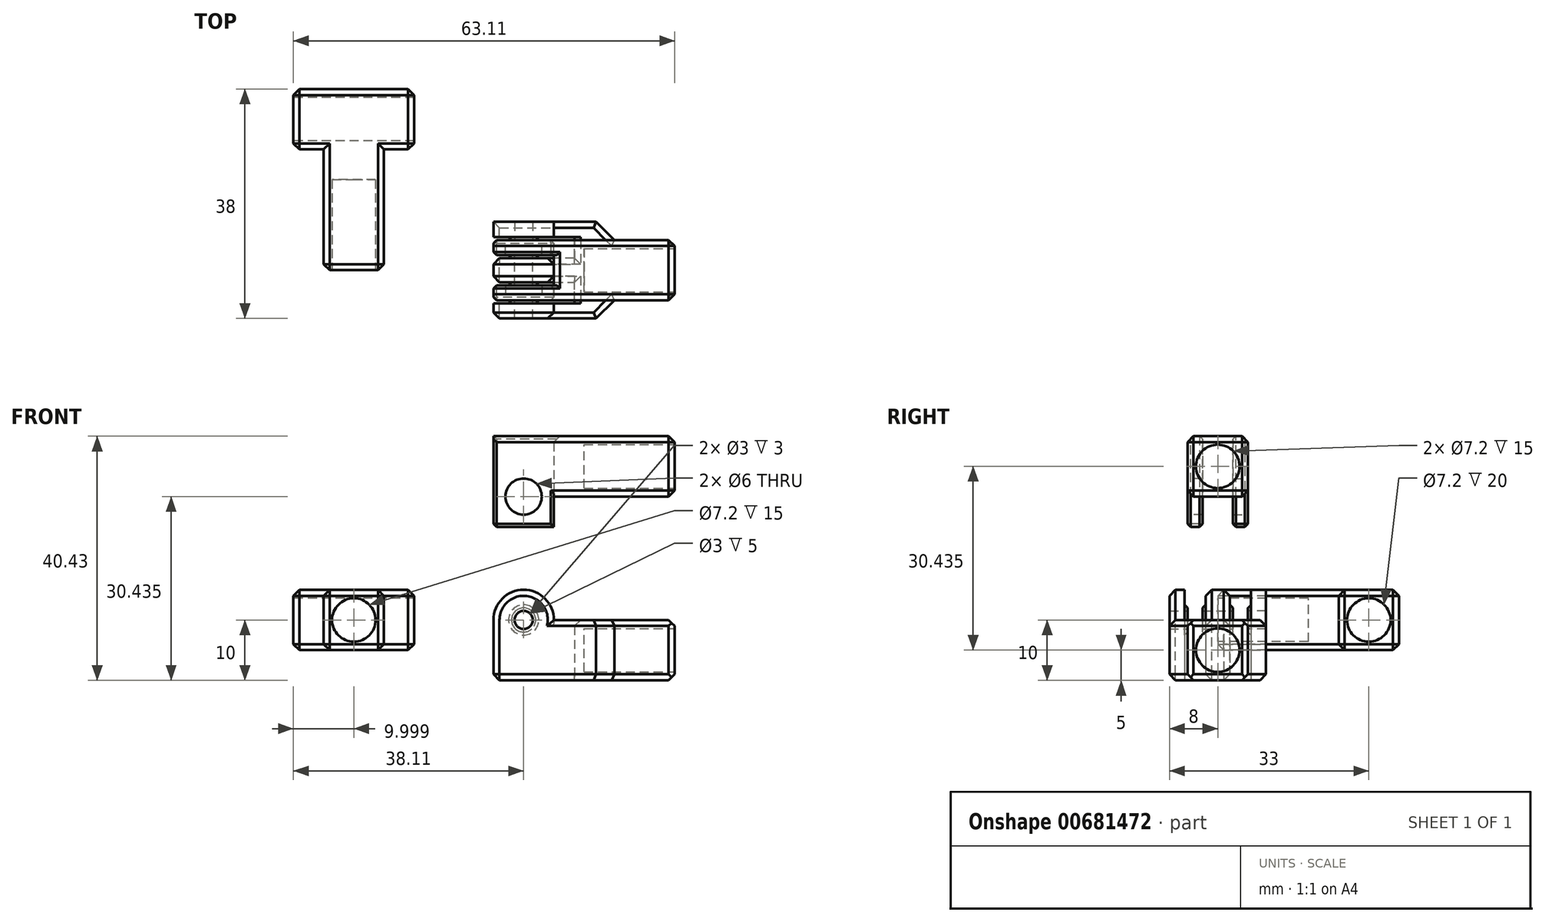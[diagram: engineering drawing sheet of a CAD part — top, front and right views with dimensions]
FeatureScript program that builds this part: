
annotation { "Feature Type Name" : "Feature", "Feature Type Description" : "" }
export const myFeature = defineFeature(function(context is Context, id is Id, definition is map)
    precondition{}
    {
        {
            var Q0;
            Q0=qCreatedBy(makeId("Front.planeOp"),FACE);
            var sketch = newSketch(context, id + "F0", { "sketchPlane" : qUnion([Q0])});
            skLineSegment(sketch, "E0.bottom", {"start": v(10, 5) * mm, "end": v(-10, 5) * mm});
            skLineSegment(sketch, "E0.top", {"start": v(10, -5) * mm, "end": v(-10, -5) * mm});
            skLineSegment(sketch, "E0.left", {"start": v(10, 5) * mm, "end": v(10, -5) * mm});
            skLineSegment(sketch, "E0.right", {"start": v(-10, 5) * mm, "end": v(-10, -5) * mm});
            skPoint(sketch, "E0.middle", {"position": v(0, 0) * mm});
            skSolve(sketch);
        }
        {
            var Q0;
            Q0 = qSketchRegion(id + "F0", true);
            extrude(context, id + "F1", {"entities" : qUnion([Q0]), "endBound" : BoundingType.SYMMETRIC, "depth" : 10 * mm, "offsetDistance" : 25 * mm});
        }
        {
            var Q0;
            Q0=qCreatedBy(makeId("Front.planeOp"),FACE);
            var sketch = newSketch(context, id + "F2", { "sketchPlane" : qUnion([Q0])});
            skLineSegment(sketch, "E1.bottom", {"start": v(-10, -5) * mm, "end": v(-20, -5) * mm});
            skLineSegment(sketch, "E1.top", {"start": v(-10, 10) * mm, "end": v(-20, 10) * mm});
            skLineSegment(sketch, "E1.left", {"start": v(-10, -5) * mm, "end": v(-10, 10) * mm});
            skLineSegment(sketch, "E1.right", {"start": v(-20, -5) * mm, "end": v(-20, 10) * mm});
            skPoint(sketch, "E2", {"position": v(-15, 5) * mm});
            skCircle(sketch, "E3", {"center": v(-15, 5) * mm, "radius": 1.5 * mm});
            skSolve(sketch);
        }
        {
            var Q0;
            Q0 = qSketchRegion(id + "F2", true);
            extrude(context, id + "F3", {"entities" : qUnion([Q0]), "operationType" : NewBodyOperationType.ADD, "endBound" : BoundingType.SYMMETRIC, "depth" : 4 * mm, "offsetDistance" : 25 * mm});
        }
        {
            var Q0;
            Q0=makeQuery(id+"F3.opExtrude","CAP_FACE",FACE,{"disambiguationData":[OSD([sQuery(id+"F2.wireOp",EDGE,"E1.bottom"),sQuery(id+"F2.wireOp",EDGE,"E1.top"),sQuery(id+"F2.wireOp",EDGE,"E1.left"),sQuery(id+"F2.wireOp",EDGE,"E1.right"),sQuery(id+"F2.wireOp",EDGE,"E3")])],"isStart":false});
            var sketch = newSketch(context, id + "F4", { "sketchPlane" : qUnion([Q0])});
            skCircle(sketch, "E4", {"center": v(-15, 5) * mm, "radius": 2.5 * mm});
            skCircle(sketch, "E5", {"center": v(-15, 5) * mm, "radius": 1.5 * mm});
            skSolve(sketch);
        }
        {
            var Q0;
            Q0 = qSketchRegion(id + "F4", true);
            extrude(context, id + "F5", {"entities" : qUnion([Q0]), "operationType" : NewBodyOperationType.ADD, "depth" : 0.5 * mm, "offsetDistance" : 25 * mm});
        }
        {
            var Q0;
            Q0=makeQuery(id+"F3.opExtrude","CAP_FACE",FACE,{"disambiguationData":[OSD([sQuery(id+"F2.wireOp",EDGE,"E1.bottom"),sQuery(id+"F2.wireOp",EDGE,"E1.top"),sQuery(id+"F2.wireOp",EDGE,"E1.left"),sQuery(id+"F2.wireOp",EDGE,"E1.right"),sQuery(id+"F2.wireOp",EDGE,"E3")])],"isStart":true});
            var sketch = newSketch(context, id + "F6", { "sketchPlane" : qUnion([Q0])});
            skCircle(sketch, "E6", {"center": v(15, 5) * mm, "radius": 2.5 * mm});
            skCircle(sketch, "E7", {"center": v(15, 5) * mm, "radius": 1.5 * mm});
            skSolve(sketch);
        }
        {
            var Q0;
            Q0 = qSketchRegion(id + "F6", true);
            extrude(context, id + "F7", {"entities" : qUnion([Q0]), "operationType" : NewBodyOperationType.ADD, "depth" : 0.5 * mm, "offsetDistance" : 25 * mm});
        }
        {
            var Q0;
            Q0=makeQuery(id+"F5.opExtrude","CAP_EDGE",EDGE,{"disambiguationData":[OSD([sQuery(id+"F4.wireOp",EDGE,"E4")])],"isStart":false});
            var Q1;
            Q1=makeQuery(id+"F7.opExtrude","CAP_EDGE",EDGE,{"disambiguationData":[OSD([sQuery(id+"F6.wireOp",EDGE,"E6")])],"isStart":false});
            chamfer(context, id + "F8", {"entities" : qUnion([Q0, Q1]), "width" : 0.5 * mm, "tangentPropagation" : true});
        }
        {
            var Q0;
            Q0=makeQuery(id+"F1.opExtrude","SWEPT_FACE",FACE,{"disambiguationData":[OSD([sQuery(id+"F0.wireOp",EDGE,"E0.left")])]});
            var sketch = newSketch(context, id + "F9", { "sketchPlane" : qUnion([Q0])});
            skCircle(sketch, "E8", {"center": v(0, 0) * mm, "radius": 3.6 * mm});
            skSolve(sketch);
        }
        {
            var Q0;
            Q0 = qSketchRegion(id + "F9", true);
            extrude(context, id + "F10", {"entities" : qUnion([Q0]), "operationType" : NewBodyOperationType.REMOVE, "oppositeDirection" : true, "depth" : 15 * mm, "offsetDistance" : 25 * mm});
        }
        {
            var Q0;
            Q0=makeQuery(id+"F1.opExtrude","CAP_EDGE",EDGE,{"disambiguationData":[OSD([sQuery(id+"F0.wireOp",EDGE,"E0.right")])],"isStart":false});
            var Q1;
            Q1=makeQuery(id+"F1.opExtrude","CAP_EDGE",EDGE,{"disambiguationData":[OSD([sQuery(id+"F0.wireOp",EDGE,"E0.right")])],"isStart":true});
            chamfer(context, id + "F11", {"entities" : qUnion([Q0, Q1]), "width" : 3 * mm, "tangentPropagation" : true});
        }
        {
            var Q0;
            Q0=makeQuery(id+"F3.opExtrude","CAP_EDGE",EDGE,{"disambiguationData":[OSD([sQuery(id+"F2.wireOp",EDGE,"E1.right")])],"isStart":false});
            var Q1;
            Q1=makeQuery(id+"F3.opExtrude","CAP_EDGE",EDGE,{"disambiguationData":[OSD([sQuery(id+"F2.wireOp",EDGE,"E1.right")])],"isStart":true});
            var Q2;
            Q2=makeQuery(id+"F1.opExtrude","CAP_EDGE",EDGE,{"disambiguationData":[OSD([sQuery(id+"F0.wireOp",EDGE,"E0.left")])],"isStart":true});
            var Q3;
            Q3=makeQuery(id+"F1.opExtrude","CAP_EDGE",EDGE,{"disambiguationData":[OSD([sQuery(id+"F0.wireOp",EDGE,"E0.left")])],"isStart":false});
            var Q4;
            Q4=makeQuery(id+"F1.opExtrude","SWEPT_EDGE",EDGE,{"disambiguationData":[OSD([sQuery(id+"F0.wireOp",EDGE,"E0.top"),sQuery(id+"F0.wireOp",EDGE,"E0.left")])]});
            var Q5;
            Q5=makeQuery(id+"F3.opExtrude","CAP_EDGE",EDGE,{"disambiguationData":[OSD([sQuery(id+"F2.wireOp",EDGE,"E1.bottom")])],"isStart":false});
            var Q6;
            Q6=makeQuery(id+"F3.opExtrude","CAP_EDGE",EDGE,{"disambiguationData":[OSD([sQuery(id+"F2.wireOp",EDGE,"E1.bottom")])],"isStart":true});
            var Q7;
            Q7=makeQuery(id+"F3.opExtrude","SWEPT_EDGE",EDGE,{"disambiguationData":[OSD([sQuery(id+"F2.wireOp",EDGE,"E1.bottom"),sQuery(id+"F2.wireOp",EDGE,"E1.right")])]});
            var Q8;
            Q8=makeQuery(id+"F1.opExtrude","SWEPT_EDGE",EDGE,{"disambiguationData":[OSD([sQuery(id+"F0.wireOp",EDGE,"E0.bottom"),sQuery(id+"F0.wireOp",EDGE,"E0.left")])]});
            chamfer(context, id + "F12", {"entities" : qUnion([Q0, Q1, Q2, Q3, Q4, Q5, Q6, Q7, Q8]), "width" : 1 * mm, "tangentPropagation" : true});
        }
        {
            var Q0;
            Q0=qCreatedBy(makeId("Front.planeOp"),FACE);
            var sketch = newSketch(context, id + "F13", { "sketchPlane" : qUnion([Q0])});
            skLineSegment(sketch, "E9.bottom", {"start": v(10, 25.43) * mm, "end": v(-10, 25.43) * mm});
            skLineSegment(sketch, "E9.top", {"start": v(10, 35.43) * mm, "end": v(-10, 35.43) * mm});
            skLineSegment(sketch, "E9.left", {"start": v(10, 25.43) * mm, "end": v(10, 35.43) * mm});
            skLineSegment(sketch, "E9.right", {"start": v(-10, 25.43) * mm, "end": v(-10, 35.43) * mm});
            skPoint(sketch, "E9.middle", {"position": v(0, 30.43) * mm});
            skSolve(sketch);
        }
        {
            var Q0;
            Q0 = qSketchRegion(id + "F13", true);
            extrude(context, id + "F14", {"entities" : qUnion([Q0]), "endBound" : BoundingType.SYMMETRIC, "depth" : 10 * mm, "offsetDistance" : 25 * mm});
        }
        {
            var Q0;
            Q0=makeQuery(id+"F14.opExtrude","CAP_FACE",FACE,{"disambiguationData":[OSD([sQuery(id+"F13.wireOp",EDGE,"E9.bottom"),sQuery(id+"F13.wireOp",EDGE,"E9.top"),sQuery(id+"F13.wireOp",EDGE,"E9.left"),sQuery(id+"F13.wireOp",EDGE,"E9.right")])],"isStart":true});
            var sketch = newSketch(context, id + "F15", { "sketchPlane" : qUnion([Q0])});
            skLineSegment(sketch, "E10.bottom", {"start": v(10, 35.43) * mm, "end": v(20, 35.43) * mm});
            skLineSegment(sketch, "E10.top", {"start": v(10, 20.43) * mm, "end": v(20, 20.43) * mm});
            skLineSegment(sketch, "E10.left", {"start": v(10, 35.43) * mm, "end": v(10, 20.43) * mm});
            skLineSegment(sketch, "E10.right", {"start": v(20, 35.43) * mm, "end": v(20, 20.43) * mm});
            skCircle(sketch, "E11", {"center": v(15, 25.43) * mm, "radius": 3 * mm});
            skSolve(sketch);
        }
        {
            var Q0;
            Q0 = qSketchRegion(id + "F15", true);
            extrude(context, id + "F16", {"entities" : qUnion([Q0]), "operationType" : NewBodyOperationType.ADD, "oppositeDirection" : true, "depth" : 2.5 * mm, "offsetDistance" : 25 * mm});
        }
        {
            var Q0;
            Q0=makeQuery(id+"F14.opExtrude","CAP_FACE",FACE,{"disambiguationData":[OSD([sQuery(id+"F13.wireOp",EDGE,"E9.bottom"),sQuery(id+"F13.wireOp",EDGE,"E9.top"),sQuery(id+"F13.wireOp",EDGE,"E9.left"),sQuery(id+"F13.wireOp",EDGE,"E9.right")])],"isStart":false});
            var sketch = newSketch(context, id + "F17", { "sketchPlane" : qUnion([Q0])});
            skLineSegment(sketch, "E12.bottom", {"start": v(-10, 35.43) * mm, "end": v(-20, 35.43) * mm});
            skLineSegment(sketch, "E12.top", {"start": v(-10, 20.43) * mm, "end": v(-20, 20.43) * mm});
            skLineSegment(sketch, "E12.left", {"start": v(-10, 35.43) * mm, "end": v(-10, 20.43) * mm});
            skLineSegment(sketch, "E12.right", {"start": v(-20, 35.43) * mm, "end": v(-20, 20.43) * mm});
            skCircle(sketch, "E13", {"center": v(-15, 25.43) * mm, "radius": 3 * mm});
            skSolve(sketch);
        }
        {
            var Q0;
            Q0 = qSketchRegion(id + "F17", true);
            extrude(context, id + "F18", {"entities" : qUnion([Q0]), "operationType" : NewBodyOperationType.ADD, "oppositeDirection" : true, "depth" : 2.5 * mm, "offsetDistance" : 25 * mm});
        }
        {
            var Q0;
            Q0=makeQuery(id+"F14.opExtrude","SWEPT_FACE",FACE,{"disambiguationData":[OSD([sQuery(id+"F13.wireOp",EDGE,"E9.left")])]});
            var sketch = newSketch(context, id + "F19", { "sketchPlane" : qUnion([Q0])});
            skCircle(sketch, "E14", {"center": v(0, 30.43) * mm, "radius": 3.6 * mm});
            skPoint(sketch, "E14.centerSnap0", {"position": v(-5, 30.43) * mm});
            skPoint(sketch, "E14.centerSnap1", {"position": v(0, 25.43) * mm});
            skSolve(sketch);
        }
        {
            var Q0;
            Q0 = qSketchRegion(id + "F19", true);
            extrude(context, id + "F20", {"entities" : qUnion([Q0]), "operationType" : NewBodyOperationType.REMOVE, "oppositeDirection" : true, "depth" : 15 * mm, "offsetDistance" : 25 * mm});
        }
        {
            var Q0;
            Q0=makeQuery(id+"F16.boolean.opBoolean","MERGE",EDGE,{"derivedFrom":[makeQuery(id+"F14.opExtrude","CAP_EDGE",EDGE,{"disambiguationData":[OSD([sQuery(id+"F13.wireOp",EDGE,"E9.top")])],"isStart":true}),makeQuery(id+"F16.opExtrude","CAP_EDGE",EDGE,{"disambiguationData":[OSD([sQuery(id+"F15.wireOp",EDGE,"E10.bottom")])],"isStart":true})]});
            var Q1;
            Q1=makeQuery(id+"F18.boolean.opBoolean","MERGE",EDGE,{"derivedFrom":[makeQuery(id+"F14.opExtrude","CAP_EDGE",EDGE,{"disambiguationData":[OSD([sQuery(id+"F13.wireOp",EDGE,"E9.top")])],"isStart":false}),makeQuery(id+"F18.opExtrude","CAP_EDGE",EDGE,{"disambiguationData":[OSD([sQuery(id+"F17.wireOp",EDGE,"E12.bottom")])],"isStart":true})]});
            var Q2;
            Q2=makeQuery(id+"F14.opExtrude","SWEPT_EDGE",EDGE,{"disambiguationData":[OSD([sQuery(id+"F13.wireOp",EDGE,"E9.top"),sQuery(id+"F13.wireOp",EDGE,"E9.left")])]});
            var Q3;
            Q3=makeQuery(id+"F14.opExtrude","SWEPT_EDGE",EDGE,{"disambiguationData":[OSD([sQuery(id+"F13.wireOp",EDGE,"E9.top"),sQuery(id+"F13.wireOp",EDGE,"E9.right")])]});
            var Q4;
            Q4=makeQuery(id+"F14.opExtrude","CAP_EDGE",EDGE,{"disambiguationData":[OSD([sQuery(id+"F13.wireOp",EDGE,"E9.bottom")])],"isStart":true});
            var Q5;
            Q5=makeQuery(id+"F14.opExtrude","CAP_EDGE",EDGE,{"disambiguationData":[OSD([sQuery(id+"F13.wireOp",EDGE,"E9.left")])],"isStart":true});
            var Q6;
            Q6=makeQuery(id+"F14.opExtrude","CAP_EDGE",EDGE,{"disambiguationData":[OSD([sQuery(id+"F13.wireOp",EDGE,"E9.bottom")])],"isStart":false});
            var Q7;
            Q7=makeQuery(id+"F14.opExtrude","CAP_EDGE",EDGE,{"disambiguationData":[OSD([sQuery(id+"F13.wireOp",EDGE,"E9.left")])],"isStart":false});
            var Q8;
            Q8=makeQuery(id+"F14.opExtrude","SWEPT_EDGE",EDGE,{"disambiguationData":[OSD([sQuery(id+"F13.wireOp",EDGE,"E9.bottom"),sQuery(id+"F13.wireOp",EDGE,"E9.left")])]});
            chamfer(context, id + "F21", {"entities" : qUnion([Q0, Q1, Q2, Q3, Q4, Q5, Q6, Q7, Q8]), "width" : 1 * mm, "tangentPropagation" : true});
        }
        {
            var Q0;
            Q0=makeQuery(id+"F18.opExtrude","CAP_EDGE",EDGE,{"disambiguationData":[OSD([sQuery(id+"F17.wireOp",EDGE,"E12.top")])],"isStart":true});
            var Q1;
            Q1=makeQuery(id+"F18.opExtrude","CAP_EDGE",EDGE,{"disambiguationData":[OSD([sQuery(id+"F17.wireOp",EDGE,"E12.top")])],"isStart":false});
            var Q2;
            Q2=makeQuery(id+"F18.opExtrude","CAP_EDGE",EDGE,{"disambiguationData":[OSD([sQuery(id+"F17.wireOp",EDGE,"E12.left")])],"isStart":true});
            var Q3;
            {var subQ0=sQuery(id+"F17.wireOp",EDGE,"E12.left");Q3=makeQuery(id+"F18.boolean.opBoolean","SPLIT",EDGE,{"disambiguationData":[topologyDisambiguationEdgeConnected([makeQuery(id+"F18.opExtrude","SWEPT_FACE",FACE,{"disambiguationData":[OSD([subQ0])]})])],"derivedFrom":makeQuery(id+"F18.opExtrude","CAP_EDGE",EDGE,{"disambiguationData":[OSD([subQ0])],"isStart":false})});}
            var Q4;
            Q4=makeQuery(id+"F18.opExtrude","CAP_EDGE",EDGE,{"disambiguationData":[OSD([sQuery(id+"F17.wireOp",EDGE,"E12.right")])],"isStart":true});
            var Q5;
            {var subQ0=sQuery(id+"F15.wireOp",EDGE,"E10.left");Q5=makeQuery(id+"F16.boolean.opBoolean","SPLIT",EDGE,{"disambiguationData":[topologyDisambiguationEdgeConnected([makeQuery(id+"F16.opExtrude","SWEPT_FACE",FACE,{"disambiguationData":[OSD([subQ0])]})])],"derivedFrom":makeQuery(id+"F16.opExtrude","CAP_EDGE",EDGE,{"disambiguationData":[OSD([subQ0])],"isStart":false})});}
            var Q6;
            Q6=makeQuery(id+"F16.opExtrude","CAP_EDGE",EDGE,{"disambiguationData":[OSD([sQuery(id+"F15.wireOp",EDGE,"E10.top")])],"isStart":false});
            var Q7;
            Q7=makeQuery(id+"F16.opExtrude","SWEPT_EDGE",EDGE,{"disambiguationData":[OSD([sQuery(id+"F15.wireOp",EDGE,"E10.top"),sQuery(id+"F15.wireOp",EDGE,"E10.left")])]});
            var Q8;
            Q8=makeQuery(id+"F16.opExtrude","CAP_EDGE",EDGE,{"disambiguationData":[OSD([sQuery(id+"F15.wireOp",EDGE,"E10.top")])],"isStart":true});
            var Q9;
            Q9=makeQuery(id+"F16.opExtrude","SWEPT_EDGE",EDGE,{"disambiguationData":[OSD([sQuery(id+"F15.wireOp",EDGE,"E10.top"),sQuery(id+"F15.wireOp",EDGE,"E10.right")])]});
            var Q10;
            Q10=makeQuery(id+"F18.opExtrude","SWEPT_EDGE",EDGE,{"disambiguationData":[OSD([sQuery(id+"F17.wireOp",EDGE,"E12.top"),sQuery(id+"F17.wireOp",EDGE,"E12.right")])]});
            var Q11;
            Q11=makeQuery(id+"F16.opExtrude","CAP_EDGE",EDGE,{"disambiguationData":[OSD([sQuery(id+"F15.wireOp",EDGE,"E10.left")])],"isStart":true});
            var Q12;
            Q12=makeQuery(id+"F16.opExtrude","CAP_EDGE",EDGE,{"disambiguationData":[OSD([sQuery(id+"F15.wireOp",EDGE,"E10.right")])],"isStart":false});
            var Q13;
            Q13=makeQuery(id+"F18.opExtrude","CAP_EDGE",EDGE,{"disambiguationData":[OSD([sQuery(id+"F17.wireOp",EDGE,"E12.right")])],"isStart":false});
            var Q14;
            Q14=makeQuery(id+"F18.opExtrude","CAP_EDGE",EDGE,{"disambiguationData":[OSD([sQuery(id+"F17.wireOp",EDGE,"E12.bottom")])],"isStart":false});
            var Q15;
            Q15=makeQuery(id+"F16.opExtrude","CAP_EDGE",EDGE,{"disambiguationData":[OSD([sQuery(id+"F15.wireOp",EDGE,"E10.bottom")])],"isStart":false});
            var Q16;
            Q16=makeQuery(id+"F16.opExtrude","CAP_EDGE",EDGE,{"disambiguationData":[OSD([sQuery(id+"F15.wireOp",EDGE,"E10.right")])],"isStart":true});
            chamfer(context, id + "F22", {"entities" : qUnion([Q0, Q1, Q2, Q3, Q4, Q5, Q6, Q7, Q8, Q9, Q10, Q11, Q12, Q13, Q14, Q15, Q16]), "width" : 0.5 * mm, "tangentPropagation" : true});
        }
        {
            var Q0;
            Q0=makeQuery(id+"F3.opExtrude","SWEPT_EDGE",EDGE,{"disambiguationData":[OSD([sQuery(id+"F2.wireOp",EDGE,"E1.top"),sQuery(id+"F2.wireOp",EDGE,"E1.left")])]});
            var Q1;
            Q1=makeQuery(id+"F3.opExtrude","SWEPT_EDGE",EDGE,{"disambiguationData":[OSD([sQuery(id+"F2.wireOp",EDGE,"E1.top"),sQuery(id+"F2.wireOp",EDGE,"E1.right")])]});
            fillet(context, id + "F23", {"entities" : qUnion([Q0, Q1]), "radius" : 5 * mm, "tangentPropagation" : true, "allowEdgeOverflow" : false});
        }
        {
            var Q0;
            {var subQ0=sQuery(id+"F2.wireOp",EDGE,"E1.left");var subQ1=sQuery(id+"F2.wireOp",EDGE,"E1.top");Q0=makeQuery(id+"F23.opFillet","BLEND_EDGE",EDGE,{"blendedFrom":[makeQuery(id+"F3.opExtrude","SWEPT_EDGE",EDGE,{"disambiguationData":[OSD([subQ1,subQ0])]}),makeQuery(id+"F3.opExtrude","CAP_FACE",FACE,{"disambiguationData":[OSD([sQuery(id+"F2.wireOp",EDGE,"E1.bottom"),subQ1,subQ0,sQuery(id+"F2.wireOp",EDGE,"E1.right"),sQuery(id+"F2.wireOp",EDGE,"E3")])],"isStart":false})],"blendedInto":[makeQuery(id+"F3.opExtrude","CAP_FACE",FACE,{"disambiguationData":[OSD([sQuery(id+"F2.wireOp",EDGE,"E1.bottom"),subQ1,subQ0,sQuery(id+"F2.wireOp",EDGE,"E1.right"),sQuery(id+"F2.wireOp",EDGE,"E3")])],"isStart":false})]});}
            var Q1;
            {var subQ0=sQuery(id+"F2.wireOp",EDGE,"E1.left");var subQ1=sQuery(id+"F2.wireOp",EDGE,"E1.top");Q1=makeQuery(id+"F23.opFillet","BLEND_EDGE",EDGE,{"blendedFrom":[makeQuery(id+"F3.opExtrude","SWEPT_EDGE",EDGE,{"disambiguationData":[OSD([subQ1,subQ0])]}),makeQuery(id+"F3.opExtrude","CAP_FACE",FACE,{"disambiguationData":[OSD([sQuery(id+"F2.wireOp",EDGE,"E1.bottom"),subQ1,subQ0,sQuery(id+"F2.wireOp",EDGE,"E1.right"),sQuery(id+"F2.wireOp",EDGE,"E3")])],"isStart":true})],"blendedInto":[makeQuery(id+"F3.opExtrude","CAP_FACE",FACE,{"disambiguationData":[OSD([sQuery(id+"F2.wireOp",EDGE,"E1.bottom"),subQ1,subQ0,sQuery(id+"F2.wireOp",EDGE,"E1.right"),sQuery(id+"F2.wireOp",EDGE,"E3")])],"isStart":true})]});}
            chamfer(context, id + "F24", {"entities" : qUnion([Q0, Q1]), "width" : 1 * mm, "tangentPropagation" : true});
        }
        {
            var Q0;
            Q0=makeQuery(id+"F1.opExtrude","CAP_FACE",FACE,{"disambiguationData":[OSD([sQuery(id+"F0.wireOp",EDGE,"E0.bottom"),sQuery(id+"F0.wireOp",EDGE,"E0.top"),sQuery(id+"F0.wireOp",EDGE,"E0.left"),sQuery(id+"F0.wireOp",EDGE,"E0.right")])],"isStart":false});
            var sketch = newSketch(context, id + "F25", { "sketchPlane" : qUnion([Q0])});
            skLineSegment(sketch, "E15.bottom", {"start": v(-6.59, 4) * mm, "end": v(-12.03, 4) * mm});
            skLineSegment(sketch, "E15.top", {"start": v(-6.59, -6.15) * mm, "end": v(-12.03, -6.15) * mm});
            skLineSegment(sketch, "E15.left", {"start": v(-6.59, 4) * mm, "end": v(-6.59, -6.15) * mm});
            skLineSegment(sketch, "E15.right", {"start": v(-12.03, 4) * mm, "end": v(-12.03, -6.15) * mm});
            skLineSegment(sketch, "E16.bottom", {"start": v(-12.03, 4) * mm, "end": v(-6.59, 4) * mm});
            skLineSegment(sketch, "E16.top", {"start": v(-12.03, 6.5) * mm, "end": v(-6.59, 6.5) * mm});
            skLineSegment(sketch, "E16.left", {"start": v(-12.03, 4) * mm, "end": v(-12.03, 6.5) * mm});
            skLineSegment(sketch, "E16.right", {"start": v(-6.59, 4) * mm, "end": v(-6.59, 6.5) * mm});
            skSolve(sketch);
        }
        {
            var Q0;
            Q0 = qSketchRegion(id + "F25", true);
            extrude(context, id + "F26", {"entities" : qUnion([Q0]), "operationType" : NewBodyOperationType.REMOVE, "oppositeDirection" : true, "depth" : 3 * mm, "offsetDistance" : 25 * mm});
        }
        {
            var Q0;
            Q0=makeQuery(id+"F1.opExtrude","CAP_FACE",FACE,{"disambiguationData":[OSD([sQuery(id+"F0.wireOp",EDGE,"E0.bottom"),sQuery(id+"F0.wireOp",EDGE,"E0.top"),sQuery(id+"F0.wireOp",EDGE,"E0.left"),sQuery(id+"F0.wireOp",EDGE,"E0.right")])],"isStart":true});
            var sketch = newSketch(context, id + "F27", { "sketchPlane" : qUnion([Q0])});
            skLineSegment(sketch, "E17.bottom", {"start": v(6.59, 4) * mm, "end": v(11.72, 4) * mm});
            skLineSegment(sketch, "E17.top", {"start": v(6.59, -6.4) * mm, "end": v(11.72, -6.4) * mm});
            skLineSegment(sketch, "E17.left", {"start": v(6.59, 4) * mm, "end": v(6.59, -6.4) * mm});
            skLineSegment(sketch, "E17.right", {"start": v(11.72, 4) * mm, "end": v(11.72, -6.4) * mm});
            skLineSegment(sketch, "E18.bottom", {"start": v(6.59, 4) * mm, "end": v(11.89, 4) * mm});
            skLineSegment(sketch, "E18.top", {"start": v(6.59, 7.88) * mm, "end": v(11.89, 7.88) * mm});
            skLineSegment(sketch, "E18.left", {"start": v(6.59, 4) * mm, "end": v(6.59, 7.88) * mm});
            skLineSegment(sketch, "E18.right", {"start": v(11.89, 4) * mm, "end": v(11.89, 7.88) * mm});
            skSolve(sketch);
        }
        {
            var Q0;
            Q0 = qSketchRegion(id + "F27", true);
            extrude(context, id + "F28", {"entities" : qUnion([Q0]), "operationType" : NewBodyOperationType.REMOVE, "oppositeDirection" : true, "depth" : 3 * mm, "offsetDistance" : 25 * mm});
        }
        {
            var Q0;
            {var subQ0=sQuery(id+"F0.wireOp",EDGE,"E0.right");var subQ1=makeQuery(id+"F1.opExtrude","CAP_FACE",FACE,{"disambiguationData":[OSD([sQuery(id+"F0.wireOp",EDGE,"E0.bottom"),sQuery(id+"F0.wireOp",EDGE,"E0.top"),sQuery(id+"F0.wireOp",EDGE,"E0.left"),subQ0])],"isStart":true});Q0=makeQuery(id+"F28.boolean.opBoolean","MERGE",EDGE,{"derivedFrom":[makeQuery(id+"F12.opChamfer","BLEND_EDGE",EDGE,{"blendedFrom":[makeQuery(id+"F11.opChamfer","BLEND_EDGE",EDGE,{"blendedFrom":[makeQuery(id+"F1.opExtrude","CAP_EDGE",EDGE,{"disambiguationData":[OSD([subQ0])],"isStart":true}),subQ1],"blendedInto":[subQ1]}),subQ1],"blendedInto":[subQ1]}),makeQuery(id+"F28.opExtrude","CAP_EDGE",EDGE,{"disambiguationData":[OSD([sQuery(id+"F27.wireOp",EDGE,"E17.left"),sQuery(id+"F27.wireOp",EDGE,"E18.left")])],"isStart":true})]});}
            var Q1;
            Q1=makeQuery(id+"F28.boolean.opBoolean","INTERSECT",EDGE,{"derivedFrom":[makeQuery(id+"F3.boolean.opBoolean","MERGE",FACE,{"derivedFrom":[makeQuery(id+"F1.opExtrude","SWEPT_FACE",FACE,{"disambiguationData":[OSD([sQuery(id+"F0.wireOp",EDGE,"E0.top")])]}),makeQuery(id+"F3.opExtrude","SWEPT_FACE",FACE,{"disambiguationData":[OSD([sQuery(id+"F2.wireOp",EDGE,"E1.bottom")])]})]}),makeQuery(id+"F28.opExtrude","CAP_FACE",FACE,{"disambiguationData":[OSD([sQuery(id+"F27.wireOp",EDGE,"E17.top"),sQuery(id+"F27.wireOp",EDGE,"E17.left"),sQuery(id+"F27.wireOp",EDGE,"E17.right"),sQuery(id+"F27.wireOp",EDGE,"E18.bottom"),sQuery(id+"F27.wireOp",EDGE,"E18.top"),sQuery(id+"F27.wireOp",EDGE,"E18.left"),sQuery(id+"F27.wireOp",EDGE,"E18.right")])],"isStart":false})]});
            var Q2;
            Q2=makeQuery(id+"F26.boolean.opBoolean","INTERSECT",EDGE,{"derivedFrom":[makeQuery(id+"F3.boolean.opBoolean","MERGE",FACE,{"derivedFrom":[makeQuery(id+"F1.opExtrude","SWEPT_FACE",FACE,{"disambiguationData":[OSD([sQuery(id+"F0.wireOp",EDGE,"E0.top")])]}),makeQuery(id+"F3.opExtrude","SWEPT_FACE",FACE,{"disambiguationData":[OSD([sQuery(id+"F2.wireOp",EDGE,"E1.bottom")])]})]}),makeQuery(id+"F26.opExtrude","CAP_FACE",FACE,{"disambiguationData":[OSD([sQuery(id+"F25.wireOp",EDGE,"E15.top"),sQuery(id+"F25.wireOp",EDGE,"E15.left"),sQuery(id+"F25.wireOp",EDGE,"E15.right"),sQuery(id+"F25.wireOp",EDGE,"E16.top"),sQuery(id+"F25.wireOp",EDGE,"E16.left"),sQuery(id+"F25.wireOp",EDGE,"E16.right")])],"isStart":false})]});
            var Q3;
            {var subQ0=sQuery(id+"F0.wireOp",EDGE,"E0.right");var subQ1=makeQuery(id+"F1.opExtrude","CAP_FACE",FACE,{"disambiguationData":[OSD([sQuery(id+"F0.wireOp",EDGE,"E0.bottom"),sQuery(id+"F0.wireOp",EDGE,"E0.top"),sQuery(id+"F0.wireOp",EDGE,"E0.left"),subQ0])],"isStart":false});Q3=makeQuery(id+"F26.boolean.opBoolean","MERGE",EDGE,{"derivedFrom":[makeQuery(id+"F12.opChamfer","BLEND_EDGE",EDGE,{"blendedFrom":[makeQuery(id+"F11.opChamfer","BLEND_EDGE",EDGE,{"blendedFrom":[makeQuery(id+"F1.opExtrude","CAP_EDGE",EDGE,{"disambiguationData":[OSD([subQ0])],"isStart":false}),subQ1],"blendedInto":[subQ1]}),subQ1],"blendedInto":[subQ1]}),makeQuery(id+"F26.opExtrude","CAP_EDGE",EDGE,{"disambiguationData":[OSD([sQuery(id+"F25.wireOp",EDGE,"E15.left"),sQuery(id+"F25.wireOp",EDGE,"E16.right")])],"isStart":true})]});}
            var Q4;
            Q4=makeQuery(id+"F28.boolean.opBoolean","INTERSECT",EDGE,{"derivedFrom":[makeQuery(id+"F1.opExtrude","SWEPT_FACE",FACE,{"disambiguationData":[OSD([sQuery(id+"F0.wireOp",EDGE,"E0.bottom")])]}),makeQuery(id+"F28.opExtrude","CAP_FACE",FACE,{"disambiguationData":[OSD([sQuery(id+"F27.wireOp",EDGE,"E17.top"),sQuery(id+"F27.wireOp",EDGE,"E17.left"),sQuery(id+"F27.wireOp",EDGE,"E17.right"),sQuery(id+"F27.wireOp",EDGE,"E18.bottom"),sQuery(id+"F27.wireOp",EDGE,"E18.top"),sQuery(id+"F27.wireOp",EDGE,"E18.left"),sQuery(id+"F27.wireOp",EDGE,"E18.right")])],"isStart":false})]});
            var Q5;
            Q5=makeQuery(id+"F26.boolean.opBoolean","INTERSECT",EDGE,{"derivedFrom":[makeQuery(id+"F1.opExtrude","SWEPT_FACE",FACE,{"disambiguationData":[OSD([sQuery(id+"F0.wireOp",EDGE,"E0.bottom")])]}),makeQuery(id+"F26.opExtrude","CAP_FACE",FACE,{"disambiguationData":[OSD([sQuery(id+"F25.wireOp",EDGE,"E15.top"),sQuery(id+"F25.wireOp",EDGE,"E15.left"),sQuery(id+"F25.wireOp",EDGE,"E15.right"),sQuery(id+"F25.wireOp",EDGE,"E16.top"),sQuery(id+"F25.wireOp",EDGE,"E16.left"),sQuery(id+"F25.wireOp",EDGE,"E16.right")])],"isStart":false})]});
            chamfer(context, id + "F29", {"entities" : qUnion([Q0, Q1, Q2, Q3, Q4, Q5]), "width" : 1 * mm, "tangentPropagation" : true});
        }
        {
            var Q0;
            Q0=makeQuery(id+"F1.opExtrude","CAP_FACE",FACE,{"disambiguationData":[OSD([sQuery(id+"F0.wireOp",EDGE,"E0.bottom"),sQuery(id+"F0.wireOp",EDGE,"E0.top"),sQuery(id+"F0.wireOp",EDGE,"E0.left"),sQuery(id+"F0.wireOp",EDGE,"E0.right")])],"isStart":false});
            var sketch = newSketch(context, id + "F30", { "sketchPlane" : qUnion([Q0])});
            skPoint(sketch, "E19", {"position": v(-15, 5) * mm});
            skCircle(sketch, "E20", {"center": v(-15, 5) * mm, "radius": 1.5 * mm});
            skLineSegment(sketch, "E21", {"start": v(0, 5) * mm, "end": v(0, -5) * mm});
            skLineSegment(sketch, "E22", {"start": v(0, -5) * mm, "end": v(-20, -5) * mm});
            skLineSegment(sketch, "E23", {"start": v(-20, -5) * mm, "end": v(-20, 10) * mm});
            skLineSegment(sketch, "E24", {"start": v(-20, 10) * mm, "end": v(-10, 10) * mm});
            skLineSegment(sketch, "E25", {"start": v(0, 5) * mm, "end": v(-10, 5) * mm});
            skLineSegment(sketch, "E26", {"start": v(-10, 10) * mm, "end": v(-10, 5) * mm});
            skSolve(sketch);
        }
        {
            var Q0;
            Q0 = qSketchRegion(id + "F30", true);
            extrude(context, id + "F31", {"entities" : qUnion([Q0]), "operationType" : NewBodyOperationType.ADD, "depth" : 3 * mm, "offsetDistance" : 25 * mm});
        }
        {
            var Q0;
            Q0=makeQuery(id+"F1.opExtrude","CAP_FACE",FACE,{"disambiguationData":[OSD([sQuery(id+"F0.wireOp",EDGE,"E0.bottom"),sQuery(id+"F0.wireOp",EDGE,"E0.top"),sQuery(id+"F0.wireOp",EDGE,"E0.left"),sQuery(id+"F0.wireOp",EDGE,"E0.right")])],"isStart":true});
            var sketch = newSketch(context, id + "F32", { "sketchPlane" : qUnion([Q0])});
            skLineSegment(sketch, "E27", {"start": v(0, 5) * mm, "end": v(0, -5) * mm});
            skLineSegment(sketch, "E28", {"start": v(0, -5) * mm, "end": v(20, -5) * mm});
            skLineSegment(sketch, "E29", {"start": v(20, -5) * mm, "end": v(20, 10) * mm});
            skLineSegment(sketch, "E30", {"start": v(20, 10) * mm, "end": v(10, 10) * mm});
            skLineSegment(sketch, "E31", {"start": v(10, 10) * mm, "end": v(10, 5) * mm});
            skLineSegment(sketch, "E32", {"start": v(10, 5) * mm, "end": v(0, 5) * mm});
            skCircle(sketch, "E33", {"center": v(15, 5) * mm, "radius": 1.5 * mm});
            skSolve(sketch);
        }
        {
            var Q0;
            Q0 = qSketchRegion(id + "F32", true);
            extrude(context, id + "F33", {"entities" : qUnion([Q0]), "operationType" : NewBodyOperationType.ADD, "depth" : 3 * mm, "offsetDistance" : 25 * mm});
        }
        {
            var Q0;
            Q0=makeQuery(id+"F33.boolean.opBoolean","MERGE",FACE,{"derivedFrom":[makeQuery(id+"F31.boolean.opBoolean","MERGE",FACE,{"derivedFrom":[makeQuery(id+"F3.boolean.opBoolean","MERGE",FACE,{"derivedFrom":[makeQuery(id+"F1.opExtrude","SWEPT_FACE",FACE,{"disambiguationData":[OSD([sQuery(id+"F0.wireOp",EDGE,"E0.top")])]}),makeQuery(id+"F3.opExtrude","SWEPT_FACE",FACE,{"disambiguationData":[OSD([sQuery(id+"F2.wireOp",EDGE,"E1.bottom")])]})]}),makeQuery(id+"F31.opExtrude","SWEPT_FACE",FACE,{"disambiguationData":[OSD([sQuery(id+"F30.wireOp",EDGE,"E22")])]})]}),makeQuery(id+"F33.opExtrude","SWEPT_FACE",FACE,{"disambiguationData":[OSD([sQuery(id+"F32.wireOp",EDGE,"E28")])]})]});
            var sketch = newSketch(context, id + "F34", { "sketchPlane" : qUnion([Q0])});
            skLineSegment(sketch, "E34.bottom", {"start": v(-20, -5) * mm, "end": v(-6.59, -5) * mm});
            skLineSegment(sketch, "E34.top", {"start": v(-20, -5.5) * mm, "end": v(-6.59, -5.5) * mm});
            skLineSegment(sketch, "E34.left", {"start": v(-20, -5) * mm, "end": v(-20, -5.5) * mm});
            skLineSegment(sketch, "E34.right", {"start": v(-6.59, -5) * mm, "end": v(-6.59, -5.5) * mm});
            skLineSegment(sketch, "E35.bottom", {"start": v(-6.59, 5) * mm, "end": v(-20, 5) * mm});
            skLineSegment(sketch, "E35.top", {"start": v(-6.59, 5.5) * mm, "end": v(-20, 5.5) * mm});
            skLineSegment(sketch, "E35.left", {"start": v(-6.59, 5) * mm, "end": v(-6.59, 5.5) * mm});
            skLineSegment(sketch, "E35.right", {"start": v(-20, 5) * mm, "end": v(-20, 5.5) * mm});
            skSolve(sketch);
        }
        {
            var Q0;
            Q0 = qSketchRegion(id + "F34", true);
            extrude(context, id + "F35", {"entities" : qUnion([Q0]), "operationType" : NewBodyOperationType.REMOVE, "oppositeDirection" : true, "depth" : 25 * mm, "offsetDistance" : 25 * mm});
        }
        {
            var Q0;
            Q0=makeQuery(id+"F35.boolean.opBoolean","COPY",FACE,{"derivedFrom":makeQuery(id+"F35.opExtrude","SWEPT_FACE",FACE,{"disambiguationData":[OSD([sQuery(id+"F34.wireOp",EDGE,"E34.top")])]})});
            var sketch = newSketch(context, id + "F36", { "sketchPlane" : qUnion([Q0])});
            skCircle(sketch, "E36", {"center": v(-15, 5) * mm, "radius": 2.5 * mm});
            skCircle(sketch, "E37", {"center": v(-15, 5) * mm, "radius": 1.5 * mm});
            skSolve(sketch);
        }
        {
            var Q0;
            Q0 = qSketchRegion(id + "F36", true);
            extrude(context, id + "F37", {"entities" : qUnion([Q0]), "operationType" : NewBodyOperationType.ADD, "depth" : 0.5 * mm, "offsetDistance" : 25 * mm});
        }
        {
            var Q0;
            Q0=makeQuery(id+"F35.boolean.opBoolean","COPY",FACE,{"derivedFrom":makeQuery(id+"F35.opExtrude","SWEPT_FACE",FACE,{"disambiguationData":[OSD([sQuery(id+"F34.wireOp",EDGE,"E35.top")])]})});
            var sketch = newSketch(context, id + "F38", { "sketchPlane" : qUnion([Q0])});
            skCircle(sketch, "E38", {"center": v(15, 5) * mm, "radius": 2.5 * mm});
            skCircle(sketch, "E39", {"center": v(15, 5) * mm, "radius": 1.5 * mm});
            skSolve(sketch);
        }
        {
            var Q0;
            Q0 = qSketchRegion(id + "F38", true);
            extrude(context, id + "F39", {"entities" : qUnion([Q0]), "operationType" : NewBodyOperationType.ADD, "depth" : 0.5 * mm, "offsetDistance" : 25 * mm});
        }
        {
            var Q0;
            Q0=makeQuery(id+"F39.opExtrude","CAP_EDGE",EDGE,{"disambiguationData":[OSD([sQuery(id+"F38.wireOp",EDGE,"E38")])],"isStart":false});
            var Q1;
            Q1=makeQuery(id+"F37.opExtrude","CAP_EDGE",EDGE,{"disambiguationData":[OSD([sQuery(id+"F36.wireOp",EDGE,"E36")])],"isStart":false});
            chamfer(context, id + "F40", {"entities" : qUnion([Q0, Q1]), "width" : 0.5 * mm, "tangentPropagation" : true});
        }
        {
            var Q0;
            Q0=makeQuery(id+"F31.opExtrude","SWEPT_EDGE",EDGE,{"disambiguationData":[OSD([sQuery(id+"F30.wireOp",EDGE,"E23"),sQuery(id+"F30.wireOp",EDGE,"E24")])]});
            var Q1;
            Q1=makeQuery(id+"F31.opExtrude","SWEPT_EDGE",EDGE,{"disambiguationData":[OSD([sQuery(id+"F30.wireOp",EDGE,"E24"),sQuery(id+"F30.wireOp",EDGE,"E26")])]});
            var Q2;
            Q2=makeQuery(id+"F33.opExtrude","SWEPT_EDGE",EDGE,{"disambiguationData":[OSD([sQuery(id+"F32.wireOp",EDGE,"E30"),sQuery(id+"F32.wireOp",EDGE,"E31")])]});
            var Q3;
            Q3=makeQuery(id+"F33.opExtrude","SWEPT_EDGE",EDGE,{"disambiguationData":[OSD([sQuery(id+"F32.wireOp",EDGE,"E29"),sQuery(id+"F32.wireOp",EDGE,"E30")])]});
            fillet(context, id + "F41", {"entities" : qUnion([Q0, Q1, Q2, Q3]), "radius" : 5 * mm, "tangentPropagation" : true, "allowEdgeOverflow" : false});
        }
        {
            var Q0;
            Q0=makeQuery(id+"F31.opExtrude","CAP_EDGE",EDGE,{"disambiguationData":[OSD([sQuery(id+"F30.wireOp",EDGE,"E23")])],"isStart":false});
            var Q1;
            Q1=makeQuery(id+"F35.boolean.opBoolean","COPY",EDGE,{"derivedFrom":makeQuery(id+"F35.opExtrude","SWEPT_EDGE",EDGE,{"disambiguationData":[OSD([sQuery(id+"F30.wireOp",EDGE,"E22"),sQuery(id+"F30.wireOp",EDGE,"E23"),sQuery(id+"F34.wireOp",EDGE,"E35.top"),sQuery(id+"F34.wireOp",EDGE,"E35.right")])]})});
            var Q2;
            Q2=makeQuery(id+"F31.opExtrude","CAP_EDGE",EDGE,{"disambiguationData":[OSD([sQuery(id+"F30.wireOp",EDGE,"E25")])],"isStart":false});
            var Q3;
            Q3=makeQuery(id+"F31.opExtrude","CAP_EDGE",EDGE,{"disambiguationData":[OSD([sQuery(id+"F30.wireOp",EDGE,"E22")])],"isStart":false});
            var Q4;
            Q4=makeQuery(id+"F35.boolean.opBoolean","COPY",EDGE,{"derivedFrom":makeQuery(id+"F35.opExtrude","SWEPT_EDGE",EDGE,{"disambiguationData":[OSD([sQuery(id+"F32.wireOp",EDGE,"E28"),sQuery(id+"F32.wireOp",EDGE,"E29"),sQuery(id+"F34.wireOp",EDGE,"E34.top"),sQuery(id+"F34.wireOp",EDGE,"E34.left")])]})});
            var Q5;
            Q5=makeQuery(id+"F41.opFillet","BLEND_EDGE",EDGE,{"blendedFrom":[makeQuery(id+"F33.opExtrude","SWEPT_EDGE",EDGE,{"disambiguationData":[OSD([sQuery(id+"F32.wireOp",EDGE,"E30"),sQuery(id+"F32.wireOp",EDGE,"E31")])]}),makeQuery(id+"F35.boolean.opBoolean","COPY",FACE,{"derivedFrom":makeQuery(id+"F35.opExtrude","SWEPT_FACE",FACE,{"disambiguationData":[OSD([sQuery(id+"F34.wireOp",EDGE,"E34.top")])]})})],"blendedInto":[makeQuery(id+"F35.boolean.opBoolean","COPY",FACE,{"derivedFrom":makeQuery(id+"F35.opExtrude","SWEPT_FACE",FACE,{"disambiguationData":[OSD([sQuery(id+"F34.wireOp",EDGE,"E34.top")])]})})]});
            var Q6;
            {var subQ0=sQuery(id+"F32.wireOp",EDGE,"E31");var subQ1=sQuery(id+"F32.wireOp",EDGE,"E30");Q6=makeQuery(id+"F41.opFillet","BLEND_EDGE",EDGE,{"blendedFrom":[makeQuery(id+"F33.opExtrude","SWEPT_EDGE",EDGE,{"disambiguationData":[OSD([subQ1,subQ0])]}),makeQuery(id+"F33.opExtrude","CAP_FACE",FACE,{"disambiguationData":[OSD([sQuery(id+"F32.wireOp",EDGE,"E27"),sQuery(id+"F32.wireOp",EDGE,"E28"),sQuery(id+"F32.wireOp",EDGE,"E29"),subQ1,subQ0,sQuery(id+"F32.wireOp",EDGE,"E32"),sQuery(id+"F32.wireOp",EDGE,"E33")])],"isStart":false})],"blendedInto":[makeQuery(id+"F33.opExtrude","CAP_FACE",FACE,{"disambiguationData":[OSD([sQuery(id+"F32.wireOp",EDGE,"E27"),sQuery(id+"F32.wireOp",EDGE,"E28"),sQuery(id+"F32.wireOp",EDGE,"E29"),subQ1,subQ0,sQuery(id+"F32.wireOp",EDGE,"E32"),sQuery(id+"F32.wireOp",EDGE,"E33")])],"isStart":false})]});}
            var Q7;
            Q7=makeQuery(id+"F35.boolean.opBoolean","COPY",EDGE,{"derivedFrom":makeQuery(id+"F35.opExtrude","CAP_EDGE",EDGE,{"disambiguationData":[OSD([sQuery(id+"F34.wireOp",EDGE,"E34.top")])],"isStart":true})});
            var Q8;
            Q8=makeQuery(id+"F33.opExtrude","CAP_EDGE",EDGE,{"disambiguationData":[OSD([sQuery(id+"F32.wireOp",EDGE,"E28")])],"isStart":false});
            var Q9;
            Q9=makeQuery(id+"F33.opExtrude","SWEPT_EDGE",EDGE,{"disambiguationData":[OSD([sQuery(id+"F32.wireOp",EDGE,"E28"),sQuery(id+"F32.wireOp",EDGE,"E29")])]});
            var Q10;
            Q10=makeQuery(id+"F31.opExtrude","SWEPT_EDGE",EDGE,{"disambiguationData":[OSD([sQuery(id+"F30.wireOp",EDGE,"E22"),sQuery(id+"F30.wireOp",EDGE,"E23")])]});
            var Q11;
            Q11=makeQuery(id+"F35.boolean.opBoolean","COPY",EDGE,{"derivedFrom":makeQuery(id+"F35.opExtrude","CAP_EDGE",EDGE,{"disambiguationData":[OSD([sQuery(id+"F34.wireOp",EDGE,"E35.top")])],"isStart":true})});
            var Q12;
            Q12=makeQuery(id+"F35.boolean.opBoolean","MERGE",EDGE,{"derivedFrom":[makeQuery(id+"F26.boolean.opBoolean","INTERSECT",EDGE,{"derivedFrom":[makeQuery(id+"F3.boolean.opBoolean","MERGE",FACE,{"derivedFrom":[makeQuery(id+"F1.opExtrude","SWEPT_FACE",FACE,{"disambiguationData":[OSD([sQuery(id+"F0.wireOp",EDGE,"E0.top")])]}),makeQuery(id+"F3.opExtrude","SWEPT_FACE",FACE,{"disambiguationData":[OSD([sQuery(id+"F2.wireOp",EDGE,"E1.bottom")])]})]}),makeQuery(id+"F26.opExtrude","SWEPT_FACE",FACE,{"disambiguationData":[OSD([sQuery(id+"F25.wireOp",EDGE,"E15.left"),sQuery(id+"F25.wireOp",EDGE,"E16.right")])]})]}),makeQuery(id+"F35.opExtrude","CAP_EDGE",EDGE,{"disambiguationData":[OSD([sQuery(id+"F34.wireOp",EDGE,"E35.left")])],"isStart":true})]});
            var Q13;
            Q13=makeQuery(id+"F35.boolean.opBoolean","MERGE",EDGE,{"derivedFrom":[makeQuery(id+"F28.boolean.opBoolean","INTERSECT",EDGE,{"derivedFrom":[makeQuery(id+"F3.boolean.opBoolean","MERGE",FACE,{"derivedFrom":[makeQuery(id+"F1.opExtrude","SWEPT_FACE",FACE,{"disambiguationData":[OSD([sQuery(id+"F0.wireOp",EDGE,"E0.top")])]}),makeQuery(id+"F3.opExtrude","SWEPT_FACE",FACE,{"disambiguationData":[OSD([sQuery(id+"F2.wireOp",EDGE,"E1.bottom")])]})]}),makeQuery(id+"F28.opExtrude","SWEPT_FACE",FACE,{"disambiguationData":[OSD([sQuery(id+"F27.wireOp",EDGE,"E17.left"),sQuery(id+"F27.wireOp",EDGE,"E18.left")])]})]}),makeQuery(id+"F35.opExtrude","CAP_EDGE",EDGE,{"disambiguationData":[OSD([sQuery(id+"F34.wireOp",EDGE,"E34.right")])],"isStart":true})]});
            var Q14;
            Q14=makeQuery(id+"F35.boolean.opBoolean","INTERSECT",EDGE,{"derivedFrom":[makeQuery(id+"F33.boolean.opBoolean","MERGE",FACE,{"derivedFrom":[makeQuery(id+"F31.boolean.opBoolean","MERGE",FACE,{"derivedFrom":[makeQuery(id+"F1.opExtrude","SWEPT_FACE",FACE,{"disambiguationData":[OSD([sQuery(id+"F0.wireOp",EDGE,"E0.bottom")])]}),makeQuery(id+"F31.opExtrude","SWEPT_FACE",FACE,{"disambiguationData":[OSD([sQuery(id+"F30.wireOp",EDGE,"E25")])]})]}),makeQuery(id+"F33.opExtrude","SWEPT_FACE",FACE,{"disambiguationData":[OSD([sQuery(id+"F32.wireOp",EDGE,"E32")])]})]}),makeQuery(id+"F35.opExtrude","SWEPT_FACE",FACE,{"disambiguationData":[OSD([sQuery(id+"F34.wireOp",EDGE,"E34.right")])]})]});
            var Q15;
            Q15=makeQuery(id+"F35.boolean.opBoolean","INTERSECT",EDGE,{"derivedFrom":[makeQuery(id+"F33.boolean.opBoolean","MERGE",FACE,{"derivedFrom":[makeQuery(id+"F31.boolean.opBoolean","MERGE",FACE,{"derivedFrom":[makeQuery(id+"F1.opExtrude","SWEPT_FACE",FACE,{"disambiguationData":[OSD([sQuery(id+"F0.wireOp",EDGE,"E0.bottom")])]}),makeQuery(id+"F31.opExtrude","SWEPT_FACE",FACE,{"disambiguationData":[OSD([sQuery(id+"F30.wireOp",EDGE,"E25")])]})]}),makeQuery(id+"F33.opExtrude","SWEPT_FACE",FACE,{"disambiguationData":[OSD([sQuery(id+"F32.wireOp",EDGE,"E32")])]})]}),makeQuery(id+"F35.opExtrude","SWEPT_FACE",FACE,{"disambiguationData":[OSD([sQuery(id+"F34.wireOp",EDGE,"E35.left")])]})]});
            var Q16;
            Q16=makeQuery(id+"F33.opExtrude","CAP_EDGE",EDGE,{"disambiguationData":[OSD([sQuery(id+"F32.wireOp",EDGE,"E32")])],"isStart":false});
            chamfer(context, id + "F42", {"entities" : qUnion([Q0, Q1, Q2, Q3, Q4, Q5, Q6, Q7, Q8, Q9, Q10, Q11, Q12, Q13, Q14, Q15, Q16]), "width" : 1 * mm, "tangentPropagation" : true});
        }
        {
            var Q0;
            Q0=makeQuery(id+"F31.opExtrude","CAP_EDGE",EDGE,{"disambiguationData":[OSD([sQuery(id+"F30.wireOp",EDGE,"E21")])],"isStart":false});
            var Q1;
            Q1=makeQuery(id+"F33.opExtrude","CAP_EDGE",EDGE,{"disambiguationData":[OSD([sQuery(id+"F32.wireOp",EDGE,"E27")])],"isStart":false});
            chamfer(context, id + "F43", {"entities" : qUnion([Q0, Q1]), "width" : 3 * mm, "tangentPropagation" : true});
        }
        {
            var Q0;
            Q0=makeQuery(id+"F1.opExtrude","CAP_EDGE",EDGE,{"disambiguationData":[OSD([sQuery(id+"F0.wireOp",EDGE,"E0.top")])],"isStart":true});
            var Q1;
            Q1=makeQuery(id+"F43.opChamfer","BLEND_EDGE",EDGE,{"blendedFrom":[makeQuery(id+"F33.opExtrude","CAP_EDGE",EDGE,{"disambiguationData":[OSD([sQuery(id+"F32.wireOp",EDGE,"E27")])],"isStart":false}),makeQuery(id+"F33.boolean.opBoolean","MERGE",FACE,{"derivedFrom":[makeQuery(id+"F31.boolean.opBoolean","MERGE",FACE,{"derivedFrom":[makeQuery(id+"F3.boolean.opBoolean","MERGE",FACE,{"derivedFrom":[makeQuery(id+"F1.opExtrude","SWEPT_FACE",FACE,{"disambiguationData":[OSD([sQuery(id+"F0.wireOp",EDGE,"E0.top")])]}),makeQuery(id+"F3.opExtrude","SWEPT_FACE",FACE,{"disambiguationData":[OSD([sQuery(id+"F2.wireOp",EDGE,"E1.bottom")])]})]}),makeQuery(id+"F31.opExtrude","SWEPT_FACE",FACE,{"disambiguationData":[OSD([sQuery(id+"F30.wireOp",EDGE,"E22")])]})]}),makeQuery(id+"F33.opExtrude","SWEPT_FACE",FACE,{"disambiguationData":[OSD([sQuery(id+"F32.wireOp",EDGE,"E28")])]})]})],"blendedInto":[makeQuery(id+"F33.boolean.opBoolean","MERGE",FACE,{"derivedFrom":[makeQuery(id+"F31.boolean.opBoolean","MERGE",FACE,{"derivedFrom":[makeQuery(id+"F3.boolean.opBoolean","MERGE",FACE,{"derivedFrom":[makeQuery(id+"F1.opExtrude","SWEPT_FACE",FACE,{"disambiguationData":[OSD([sQuery(id+"F0.wireOp",EDGE,"E0.top")])]}),makeQuery(id+"F3.opExtrude","SWEPT_FACE",FACE,{"disambiguationData":[OSD([sQuery(id+"F2.wireOp",EDGE,"E1.bottom")])]})]}),makeQuery(id+"F31.opExtrude","SWEPT_FACE",FACE,{"disambiguationData":[OSD([sQuery(id+"F30.wireOp",EDGE,"E22")])]})]}),makeQuery(id+"F33.opExtrude","SWEPT_FACE",FACE,{"disambiguationData":[OSD([sQuery(id+"F32.wireOp",EDGE,"E28")])]})]})]});
            var Q2;
            Q2=makeQuery(id+"F1.opExtrude","CAP_EDGE",EDGE,{"disambiguationData":[OSD([sQuery(id+"F0.wireOp",EDGE,"E0.top")])],"isStart":false});
            var Q3;
            Q3=makeQuery(id+"F43.opChamfer","BLEND_EDGE",EDGE,{"blendedFrom":[makeQuery(id+"F31.opExtrude","CAP_EDGE",EDGE,{"disambiguationData":[OSD([sQuery(id+"F30.wireOp",EDGE,"E21")])],"isStart":false}),makeQuery(id+"F33.boolean.opBoolean","MERGE",FACE,{"derivedFrom":[makeQuery(id+"F31.boolean.opBoolean","MERGE",FACE,{"derivedFrom":[makeQuery(id+"F3.boolean.opBoolean","MERGE",FACE,{"derivedFrom":[makeQuery(id+"F1.opExtrude","SWEPT_FACE",FACE,{"disambiguationData":[OSD([sQuery(id+"F0.wireOp",EDGE,"E0.top")])]}),makeQuery(id+"F3.opExtrude","SWEPT_FACE",FACE,{"disambiguationData":[OSD([sQuery(id+"F2.wireOp",EDGE,"E1.bottom")])]})]}),makeQuery(id+"F31.opExtrude","SWEPT_FACE",FACE,{"disambiguationData":[OSD([sQuery(id+"F30.wireOp",EDGE,"E22")])]})]}),makeQuery(id+"F33.opExtrude","SWEPT_FACE",FACE,{"disambiguationData":[OSD([sQuery(id+"F32.wireOp",EDGE,"E28")])]})]})],"blendedInto":[makeQuery(id+"F33.boolean.opBoolean","MERGE",FACE,{"derivedFrom":[makeQuery(id+"F31.boolean.opBoolean","MERGE",FACE,{"derivedFrom":[makeQuery(id+"F3.boolean.opBoolean","MERGE",FACE,{"derivedFrom":[makeQuery(id+"F1.opExtrude","SWEPT_FACE",FACE,{"disambiguationData":[OSD([sQuery(id+"F0.wireOp",EDGE,"E0.top")])]}),makeQuery(id+"F3.opExtrude","SWEPT_FACE",FACE,{"disambiguationData":[OSD([sQuery(id+"F2.wireOp",EDGE,"E1.bottom")])]})]}),makeQuery(id+"F31.opExtrude","SWEPT_FACE",FACE,{"disambiguationData":[OSD([sQuery(id+"F30.wireOp",EDGE,"E22")])]})]}),makeQuery(id+"F33.opExtrude","SWEPT_FACE",FACE,{"disambiguationData":[OSD([sQuery(id+"F32.wireOp",EDGE,"E28")])]})]})]});
            var Q4;
            Q4=makeQuery(id+"F1.opExtrude","CAP_EDGE",EDGE,{"disambiguationData":[OSD([sQuery(id+"F0.wireOp",EDGE,"E0.bottom")])],"isStart":true});
            var Q5;
            Q5=makeQuery(id+"F1.opExtrude","CAP_EDGE",EDGE,{"disambiguationData":[OSD([sQuery(id+"F0.wireOp",EDGE,"E0.bottom")])],"isStart":false});
            var Q6;
            Q6=makeQuery(id+"F43.opChamfer","BLEND_EDGE",EDGE,{"blendedFrom":[makeQuery(id+"F33.opExtrude","CAP_EDGE",EDGE,{"disambiguationData":[OSD([sQuery(id+"F32.wireOp",EDGE,"E27")])],"isStart":false}),makeQuery(id+"F33.boolean.opBoolean","MERGE",FACE,{"derivedFrom":[makeQuery(id+"F31.boolean.opBoolean","MERGE",FACE,{"derivedFrom":[makeQuery(id+"F1.opExtrude","SWEPT_FACE",FACE,{"disambiguationData":[OSD([sQuery(id+"F0.wireOp",EDGE,"E0.bottom")])]}),makeQuery(id+"F31.opExtrude","SWEPT_FACE",FACE,{"disambiguationData":[OSD([sQuery(id+"F30.wireOp",EDGE,"E25")])]})]}),makeQuery(id+"F33.opExtrude","SWEPT_FACE",FACE,{"disambiguationData":[OSD([sQuery(id+"F32.wireOp",EDGE,"E32")])]})]})],"blendedInto":[makeQuery(id+"F33.boolean.opBoolean","MERGE",FACE,{"derivedFrom":[makeQuery(id+"F31.boolean.opBoolean","MERGE",FACE,{"derivedFrom":[makeQuery(id+"F1.opExtrude","SWEPT_FACE",FACE,{"disambiguationData":[OSD([sQuery(id+"F0.wireOp",EDGE,"E0.bottom")])]}),makeQuery(id+"F31.opExtrude","SWEPT_FACE",FACE,{"disambiguationData":[OSD([sQuery(id+"F30.wireOp",EDGE,"E25")])]})]}),makeQuery(id+"F33.opExtrude","SWEPT_FACE",FACE,{"disambiguationData":[OSD([sQuery(id+"F32.wireOp",EDGE,"E32")])]})]})]});
            var Q7;
            Q7=makeQuery(id+"F43.opChamfer","BLEND_EDGE",EDGE,{"blendedFrom":[makeQuery(id+"F31.opExtrude","CAP_EDGE",EDGE,{"disambiguationData":[OSD([sQuery(id+"F30.wireOp",EDGE,"E21")])],"isStart":false}),makeQuery(id+"F33.boolean.opBoolean","MERGE",FACE,{"derivedFrom":[makeQuery(id+"F31.boolean.opBoolean","MERGE",FACE,{"derivedFrom":[makeQuery(id+"F1.opExtrude","SWEPT_FACE",FACE,{"disambiguationData":[OSD([sQuery(id+"F0.wireOp",EDGE,"E0.bottom")])]}),makeQuery(id+"F31.opExtrude","SWEPT_FACE",FACE,{"disambiguationData":[OSD([sQuery(id+"F30.wireOp",EDGE,"E25")])]})]}),makeQuery(id+"F33.opExtrude","SWEPT_FACE",FACE,{"disambiguationData":[OSD([sQuery(id+"F32.wireOp",EDGE,"E32")])]})]})],"blendedInto":[makeQuery(id+"F33.boolean.opBoolean","MERGE",FACE,{"derivedFrom":[makeQuery(id+"F31.boolean.opBoolean","MERGE",FACE,{"derivedFrom":[makeQuery(id+"F1.opExtrude","SWEPT_FACE",FACE,{"disambiguationData":[OSD([sQuery(id+"F0.wireOp",EDGE,"E0.bottom")])]}),makeQuery(id+"F31.opExtrude","SWEPT_FACE",FACE,{"disambiguationData":[OSD([sQuery(id+"F30.wireOp",EDGE,"E25")])]})]}),makeQuery(id+"F33.opExtrude","SWEPT_FACE",FACE,{"disambiguationData":[OSD([sQuery(id+"F32.wireOp",EDGE,"E32")])]})]})]});
            chamfer(context, id + "F44", {"entities" : qUnion([Q0, Q1, Q2, Q3, Q4, Q5, Q6, Q7]), "width" : 1 * mm, "tangentPropagation" : true});
        }
        {
            var Q0;
            Q0=qCreatedBy(makeId("Top.planeOp"),FACE);
            var sketch = newSketch(context, id + "F45", { "sketchPlane" : qUnion([Q0])});
            skLineSegment(sketch, "E40", {"start": v(-48.11, 0) * mm, "end": v(-48.11, 20) * mm});
            skLineSegment(sketch, "E41", {"start": v(-48.11, 20) * mm, "end": v(-53.11, 20) * mm});
            skLineSegment(sketch, "E42", {"start": v(-53.11, 20) * mm, "end": v(-53.11, 30) * mm});
            skLineSegment(sketch, "E43", {"start": v(-53.11, 30) * mm, "end": v(-33.11, 30) * mm});
            skLineSegment(sketch, "E44", {"start": v(-33.11, 30) * mm, "end": v(-33.11, 20) * mm});
            skLineSegment(sketch, "E45", {"start": v(-33.11, 20) * mm, "end": v(-38.11, 20) * mm});
            skLineSegment(sketch, "E46", {"start": v(-38.11, 20) * mm, "end": v(-38.11, 0) * mm});
            skLineSegment(sketch, "E47", {"start": v(-38.11, 0) * mm, "end": v(-48.11, 0) * mm});
            skSolve(sketch);
        }
        {
            var Q0;
            Q0 = qSketchRegion(id + "F45", true);
            extrude(context, id + "F46", {"entities" : qUnion([Q0]), "depth" : 10 * mm, "offsetDistance" : 25 * mm});
        }
        {
            var Q0;
            Q0=makeQuery(id+"F46.opExtrude","SWEPT_FACE",FACE,{"disambiguationData":[OSD([sQuery(id+"F45.wireOp",EDGE,"E47")])]});
            var sketch = newSketch(context, id + "F47", { "sketchPlane" : qUnion([Q0])});
            skCircle(sketch, "E48", {"center": v(-43.11, 5) * mm, "radius": 3.6 * mm});
            skPoint(sketch, "E48.centerSnap0", {"position": v(-43.11, 0) * mm});
            skSolve(sketch);
        }
        {
            var Q0;
            Q0 = qSketchRegion(id + "F47", true);
            extrude(context, id + "F48", {"entities" : qUnion([Q0]), "operationType" : NewBodyOperationType.REMOVE, "oppositeDirection" : true, "depth" : 15 * mm, "offsetDistance" : 25 * mm});
        }
        {
            var Q0;
            Q0=makeQuery(id+"F46.opExtrude","SWEPT_FACE",FACE,{"disambiguationData":[OSD([sQuery(id+"F45.wireOp",EDGE,"E42")])]});
            var sketch = newSketch(context, id + "F49", { "sketchPlane" : qUnion([Q0])});
            skCircle(sketch, "E49", {"center": v(-25, 5) * mm, "radius": 3.6 * mm});
            skPoint(sketch, "E49.centerSnap0", {"position": v(-20, 5) * mm});
            skSolve(sketch);
        }
        {
            var Q0;
            Q0 = qSketchRegion(id + "F49", true);
            extrude(context, id + "F50", {"entities" : qUnion([Q0]), "operationType" : NewBodyOperationType.REMOVE, "oppositeDirection" : true, "depth" : 25 * mm, "offsetDistance" : 25 * mm});
        }
        {
            var Q0;
            Q0=makeQuery(id+"F46.opExtrude","CAP_FACE",FACE,{"disambiguationData":[OSD([sQuery(id+"F45.wireOp",EDGE,"E40"),sQuery(id+"F45.wireOp",EDGE,"E41"),sQuery(id+"F45.wireOp",EDGE,"E42"),sQuery(id+"F45.wireOp",EDGE,"E43"),sQuery(id+"F45.wireOp",EDGE,"E44"),sQuery(id+"F45.wireOp",EDGE,"E45"),sQuery(id+"F45.wireOp",EDGE,"E46"),sQuery(id+"F45.wireOp",EDGE,"E47")])],"isStart":false});
            var Q1;
            Q1=makeQuery(id+"F46.opExtrude","CAP_FACE",FACE,{"disambiguationData":[OSD([sQuery(id+"F45.wireOp",EDGE,"E40"),sQuery(id+"F45.wireOp",EDGE,"E41"),sQuery(id+"F45.wireOp",EDGE,"E42"),sQuery(id+"F45.wireOp",EDGE,"E43"),sQuery(id+"F45.wireOp",EDGE,"E44"),sQuery(id+"F45.wireOp",EDGE,"E45"),sQuery(id+"F45.wireOp",EDGE,"E46"),sQuery(id+"F45.wireOp",EDGE,"E47")])],"isStart":true});
            var Q2;
            Q2=makeQuery(id+"F46.opExtrude","SWEPT_EDGE",EDGE,{"disambiguationData":[OSD([sQuery(id+"F45.wireOp",EDGE,"E42"),sQuery(id+"F45.wireOp",EDGE,"E43")])]});
            var Q3;
            Q3=makeQuery(id+"F46.opExtrude","SWEPT_EDGE",EDGE,{"disambiguationData":[OSD([sQuery(id+"F45.wireOp",EDGE,"E43"),sQuery(id+"F45.wireOp",EDGE,"E44")])]});
            var Q4;
            Q4=makeQuery(id+"F46.opExtrude","SWEPT_EDGE",EDGE,{"disambiguationData":[OSD([sQuery(id+"F45.wireOp",EDGE,"E44"),sQuery(id+"F45.wireOp",EDGE,"E45")])]});
            var Q5;
            Q5=makeQuery(id+"F46.opExtrude","SWEPT_EDGE",EDGE,{"disambiguationData":[OSD([sQuery(id+"F45.wireOp",EDGE,"E46"),sQuery(id+"F45.wireOp",EDGE,"E47")])]});
            var Q6;
            Q6=makeQuery(id+"F46.opExtrude","SWEPT_EDGE",EDGE,{"disambiguationData":[OSD([sQuery(id+"F45.wireOp",EDGE,"E41"),sQuery(id+"F45.wireOp",EDGE,"E42")])]});
            var Q7;
            Q7=makeQuery(id+"F46.opExtrude","SWEPT_EDGE",EDGE,{"disambiguationData":[OSD([sQuery(id+"F45.wireOp",EDGE,"E40"),sQuery(id+"F45.wireOp",EDGE,"E47")])]});
            chamfer(context, id + "F51", {"entities" : qUnion([Q0, Q1, Q2, Q3, Q4, Q5, Q6, Q7]), "width" : 1 * mm, "tangentPropagation" : true});
        }
    });
